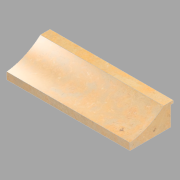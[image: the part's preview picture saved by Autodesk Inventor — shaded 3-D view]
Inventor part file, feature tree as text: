
AUTODESK INVENTOR PART (.ipt)
format: ipt  version: 2022.2 (Build 262287010, 287A)  size: 142,848 bytes
history: native  units: in
note: dims shown in document units (in); Inventor stores cm internally (conversion verified against a paired STEP export)
features: revolve x2, direct_edit x1
ambient origin geometry x8: Origin, YZ Plane, XZ Plane, XY Plane, X Axis, Y Axis, Z Axis, Center Point
bodies: Solid1 (feature_tree), Body1 (feature_tree)
feature tree (3):
  direct_edit  "Direct Edit1"
  revolve  "Rotate1"  [1 undecoded]
  revolve  "Rotate2"  [1 undecoded]
note: 2 required parameter values undecoded (feature->parameter linkage not recoverable at this tier; creation-order binding heuristic only, values carry confidence <= 0.55)
